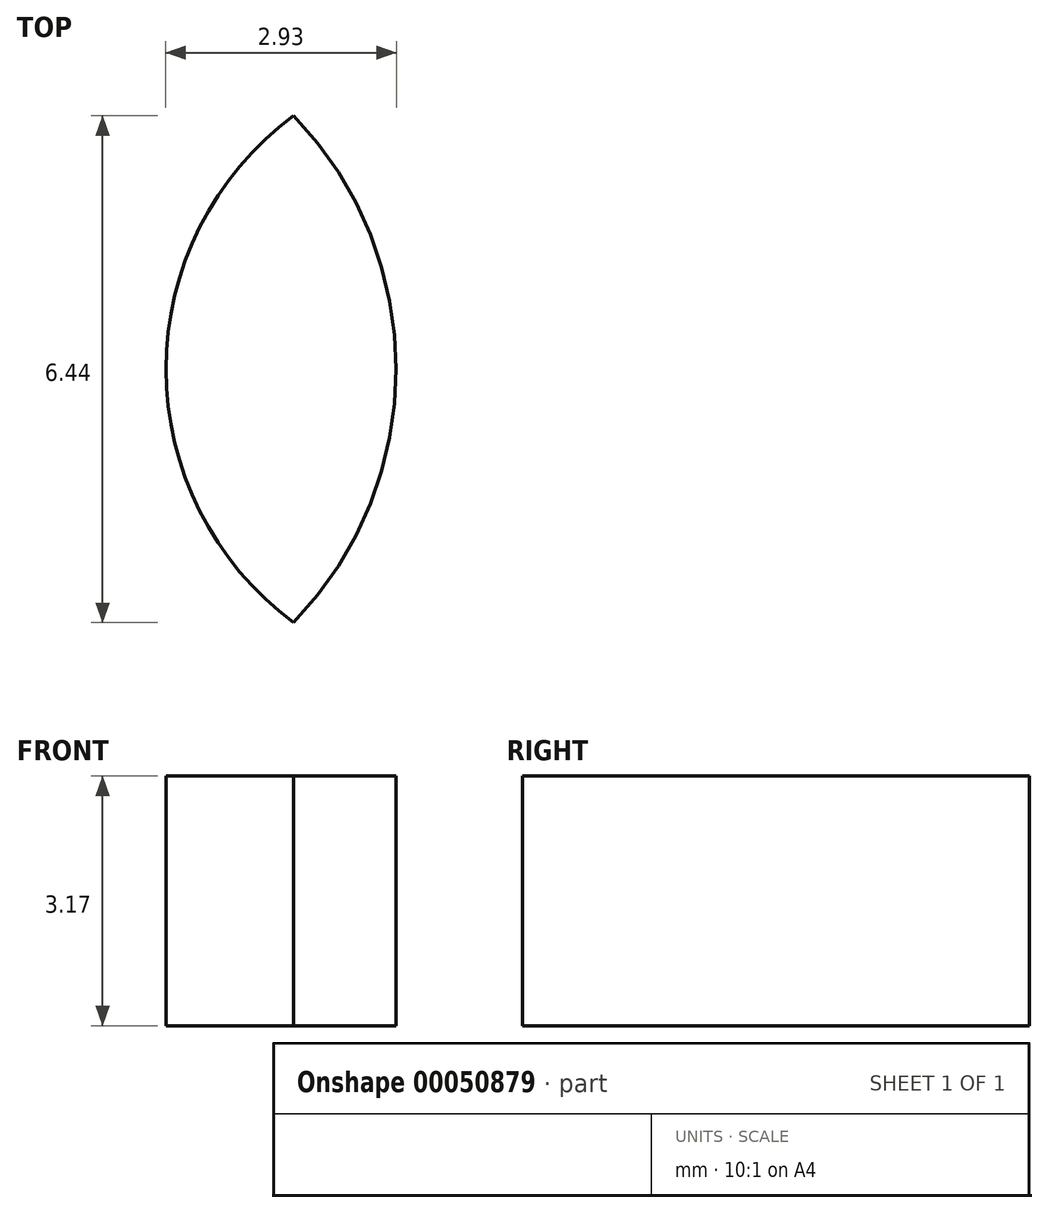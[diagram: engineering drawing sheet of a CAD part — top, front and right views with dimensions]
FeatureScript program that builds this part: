
annotation { "Feature Type Name" : "Feature", "Feature Type Description" : "" }
export const myFeature = defineFeature(function(context is Context, id is Id, definition is map)
    precondition{}
    {
        {
            var Q0;
            Q0=qCreatedBy(makeId("Top.planeOp"),FACE);
            var sketch = newSketch(context, id + "F0", { "sketchPlane" : qUnion([Q0])});
            skArc(sketch, "E0", {"start": v(0.9, -3.22) * mm, "mid": v(2.2, 0) * mm, "end": v(0.9, 3.22) * mm});
            skPoint(sketch, "E1", {"position": v(0.9, 3.22) * mm});
            skPoint(sketch, "E2", {"position": v(0.9, -3.22) * mm});
            skArc(sketch, "E3", {"start": v(0.9, 3.22) * mm, "mid": v(-0.72, 0) * mm, "end": v(0.9, -3.22) * mm});
            skSolve(sketch);
        }
        {
            var Q0;
            Q0 = qSketchRegion(id + "F0", true);
            extrude(context, id + "F1", {"entities" : qUnion([Q0]), "depth" : 3.17 * mm});
        }
    });
